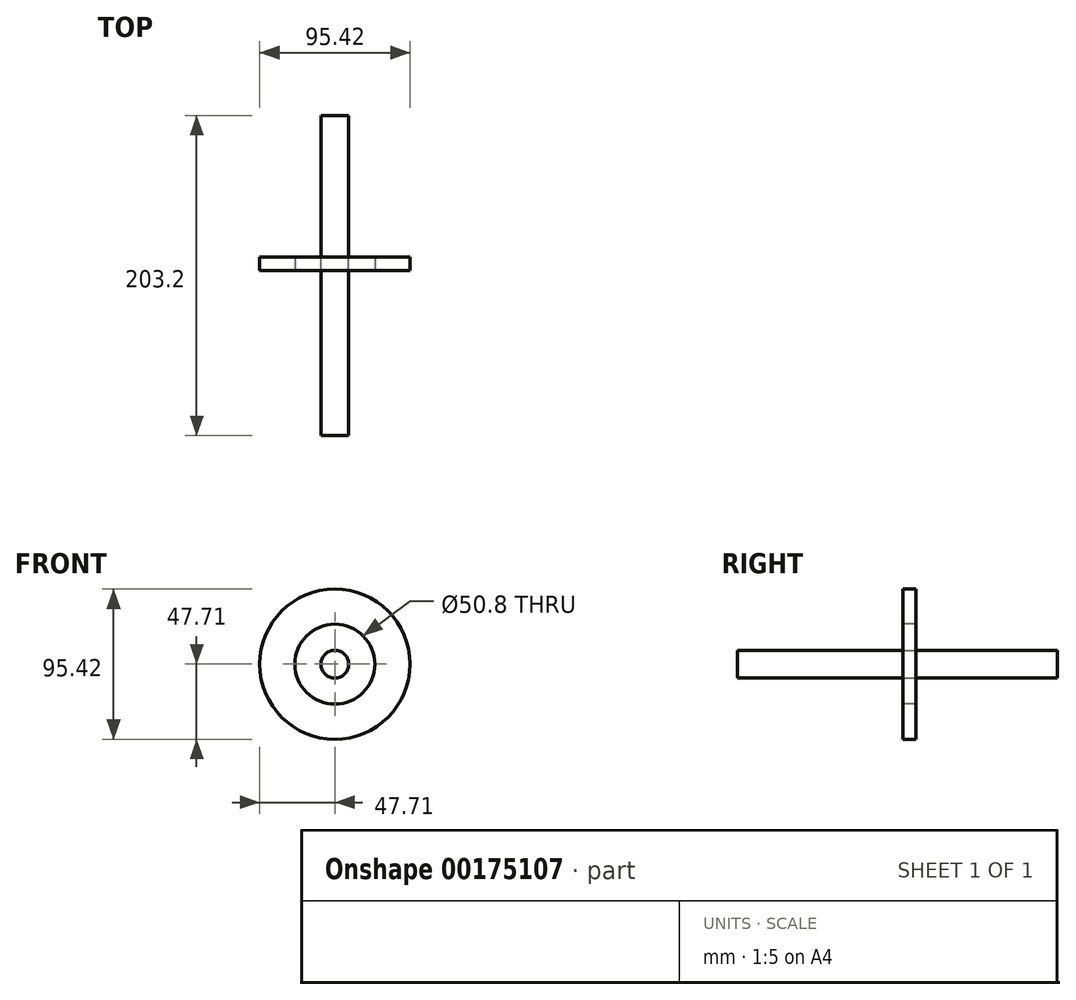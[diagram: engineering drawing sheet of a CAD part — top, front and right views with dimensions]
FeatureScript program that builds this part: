
annotation { "Feature Type Name" : "Feature", "Feature Type Description" : "" }
export const myFeature = defineFeature(function(context is Context, id is Id, definition is map)
    precondition{}
    {
        {
            var Q0;
            Q0=qCreatedBy(makeId("Front.planeOp"),FACE);
            var sketch = newSketch(context, id + "F0", { "sketchPlane" : qUnion([Q0])});
            skCircle(sketch, "E0", {"center": v(0, 0) * mm, "radius": 8.84 * mm});
            skSolve(sketch);
        }
        {
            var Q0;
            Q0=makeQuery(id+"F0.imprint","IMPRINT",FACE,{"disambiguationData":[TD([[makeQuery(id+"F0.imprint","IMPRINT",EDGE,{"derivedFrom":sQuery(id+"F0.wireOp",EDGE,"E0")}),1.0]])]});
            extrude(context, id + "F1", {"entities" : qUnion([Q0]), "endBound" : BoundingType.SYMMETRIC, "depth" : 203.2 * mm});
        }
        {
            var Q0;
            Q0=qCreatedBy(makeId("Right.planeOp"),FACE);
            var sketch = newSketch(context, id + "F2", { "sketchPlane" : qUnion([Q0])});
            skLineSegment(sketch, "E1.bottom", {"start": v(20.55, 25.4) * mm, "end": v(-28.19, 25.4) * mm});
            skLineSegment(sketch, "E1.top", {"start": v(20.55, 9.54) * mm, "end": v(-28.19, 9.54) * mm});
            skLineSegment(sketch, "E1.left", {"start": v(20.55, 25.4) * mm, "end": v(20.55, 9.54) * mm});
            skLineSegment(sketch, "E1.right", {"start": v(-28.19, 25.4) * mm, "end": v(-28.19, 9.54) * mm});
            skLineSegment(sketch, "E2.bottom", {"start": v(11.16, 47.71) * mm, "end": v(11.74, 47.71) * mm});
            skLineSegment(sketch, "E2.top", {"start": v(11.16, 43.3) * mm, "end": v(11.74, 43.3) * mm});
            skLineSegment(sketch, "E2.left", {"start": v(11.16, 47.71) * mm, "end": v(11.16, 43.3) * mm});
            skLineSegment(sketch, "E2.right", {"start": v(11.74, 47.71) * mm, "end": v(11.74, 43.3) * mm});
            skLineSegment(sketch, "E3.bottom", {"start": v(3.23, 25.4) * mm, "end": v(11.74, 25.4) * mm});
            skLineSegment(sketch, "E3.top", {"start": v(3.23, 47.71) * mm, "end": v(11.74, 47.71) * mm});
            skLineSegment(sketch, "E3.left", {"start": v(3.23, 25.4) * mm, "end": v(3.23, 47.71) * mm});
            skLineSegment(sketch, "E3.right", {"start": v(11.74, 25.4) * mm, "end": v(11.74, 47.71) * mm});
            skLineSegment(sketch, "E4.bottom", {"start": v(-11.74, 25.4) * mm, "end": v(-19.67, 25.4) * mm});
            skLineSegment(sketch, "E4.top", {"start": v(-11.74, 47.71) * mm, "end": v(-19.67, 47.71) * mm});
            skLineSegment(sketch, "E4.left", {"start": v(-11.74, 25.4) * mm, "end": v(-11.74, 47.71) * mm});
            skLineSegment(sketch, "E4.right", {"start": v(-19.67, 25.4) * mm, "end": v(-19.67, 47.71) * mm});
            skSolve(sketch);
        }
        {
            var Q0;
            {var subQ0=sQuery(id+"F2.wireOp",EDGE,"E2.top");Q0=makeQuery(id+"F2.imprint","IMPRINT",FACE,{"disambiguationData":[TD([[makeQuery(id+"F2.imprint","IMPRINT",EDGE,{"derivedFrom":subQ0}),1.0]])]});}
            var Q1;
            Q1=makeQuery(id+"F2.imprint","IMPRINT",FACE,{"disambiguationData":[TD([[makeQuery(id+"F2.imprint","IMPRINT",EDGE,{"derivedFrom":sQuery(id+"F2.wireOp",EDGE,"E4.bottom")}),-1.0]])]});
            var Q2;
            {var subQ4=sQuery(id+"F2.wireOp",EDGE,"E2.top");Q2=makeQuery(id+"F2.imprint","IMPRINT",FACE,{"disambiguationData":[TD([[makeQuery(id+"F2.imprint","IMPRINT",EDGE,{"derivedFrom":subQ4}),-1.0]])]});}
            var Q3;
            Q3=makeQuery(id+"F1.opExtrude","SWEPT_FACE",FACE,{"disambiguationData":[OSD([sQuery(id+"F0.wireOp",EDGE,"E0")])]});
            revolve(context, id + "F3", {"entities" : qUnion([Q0, Q1, Q2]), "axis" : qUnion([Q3]), "revolveType" : RevolveType.FULL});
        }
    });
